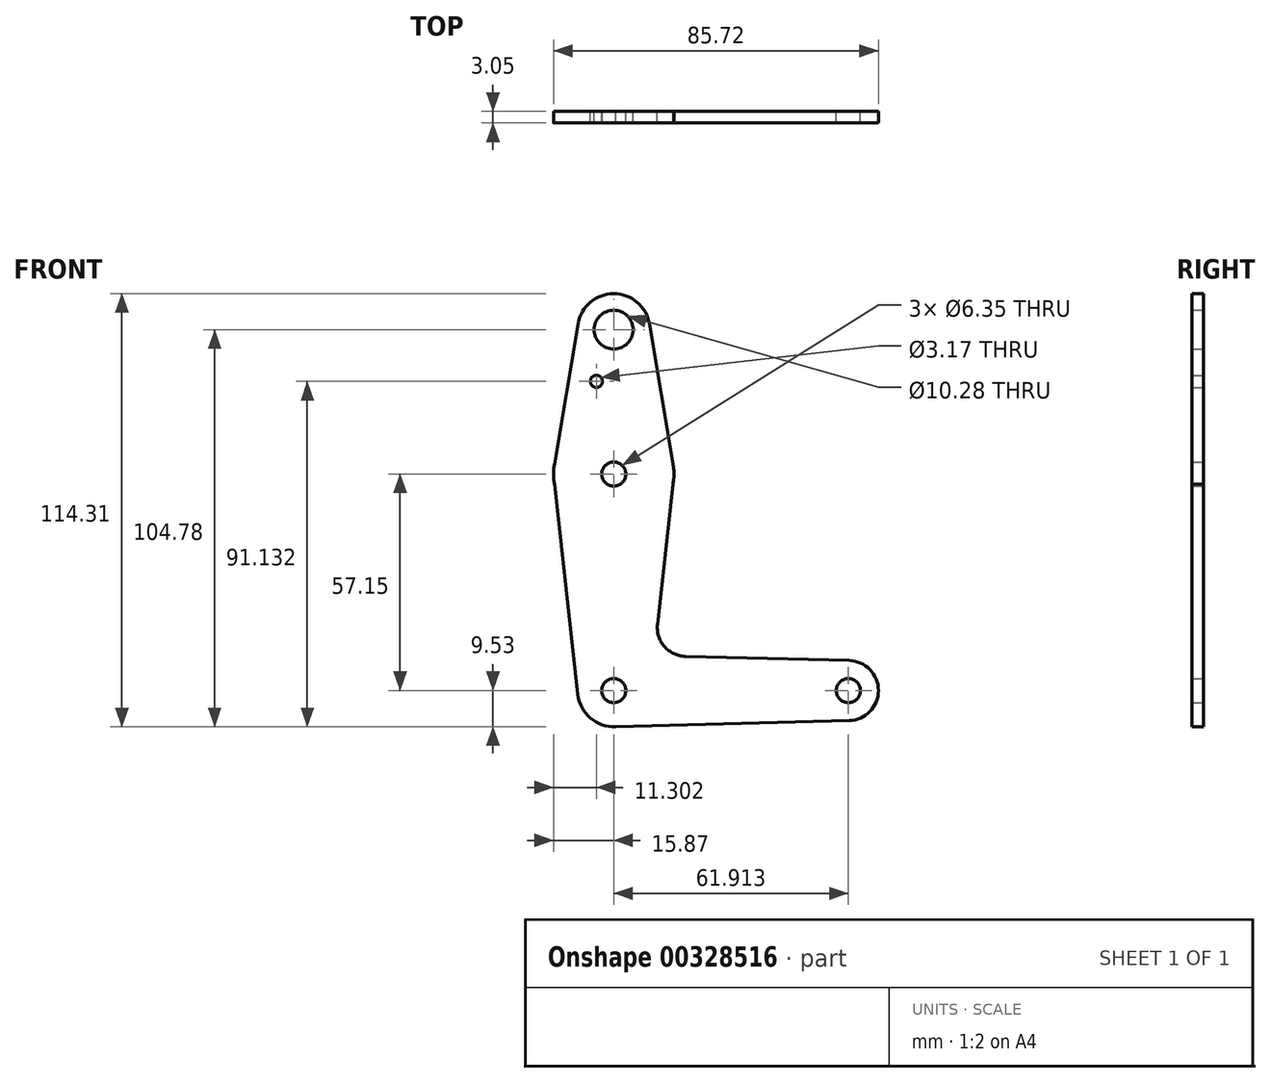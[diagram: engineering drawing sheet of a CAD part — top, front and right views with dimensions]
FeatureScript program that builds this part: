
annotation { "Feature Type Name" : "Feature", "Feature Type Description" : "" }
export const myFeature = defineFeature(function(context is Context, id is Id, definition is map)
    precondition{}
    {
        {
            var Q0;
            Q0=qCreatedBy(makeId("Front.planeOp"),FACE);
            var sketch = newSketch(context, id + "F0", { "sketchPlane" : qUnion([Q0])});
            skLineSegment(sketch, "E0", {"start": v(0, 0) * mm, "end": v(0, 95.25) * mm, "construction": true});
            skLineSegment(sketch, "E1", {"start": v(0, 0) * mm, "end": v(61.91, 0) * mm, "construction": true});
            skCircle(sketch, "E2", {"center": v(0, 95.25) * mm, "radius": 9.53 * mm});
            skCircle(sketch, "E3", {"center": v(0, 57.15) * mm, "radius": 15.88 * mm});
            skCircle(sketch, "E4", {"center": v(0, 0) * mm, "radius": 9.53 * mm});
            skCircle(sketch, "E5", {"center": v(61.91, 0) * mm, "radius": 7.94 * mm});
            skLineSegment(sketch, "E6", {"start": v(9.4, 96.84) * mm, "end": v(15.65, 59.8) * mm});
            skLineSegment(sketch, "E7", {"start": v(-15.65, 59.8) * mm, "end": v(-9.4, 96.84) * mm});
            skLineSegment(sketch, "E8", {"start": v(-15.65, 54.5) * mm, "end": v(-9.47, -1.05) * mm});
            skLineSegment(sketch, "E9", {"start": v(15.65, 54.5) * mm, "end": v(11.53, 17.5) * mm});
            skLineSegment(sketch, "E10", {"start": v(18.91, 9.04) * mm, "end": v(62.12, 7.93) * mm});
            skLineSegment(sketch, "E11", {"start": v(0, -9.52) * mm, "end": v(62.12, -7.93) * mm});
            skPoint(sketch, "E12.newPointA", {"position": v(9.47, -1.05) * mm});
            skArc(sketch, "E12.filletArc", {"start": v(11.53, 17.5) * mm, "mid": v(13.36, 11.65) * mm, "end": v(18.91, 9.04) * mm});
            skCircle(sketch, "E13", {"center": v(0, 95.25) * mm, "radius": 5.14 * mm});
            skCircle(sketch, "E14", {"center": v(-4.57, 81.6) * mm, "radius": 1.59 * mm});
            skCircle(sketch, "E15", {"center": v(0, 57.15) * mm, "radius": 3.18 * mm});
            skCircle(sketch, "E16", {"center": v(0, 0) * mm, "radius": 3.17 * mm});
            skCircle(sketch, "E17", {"center": v(61.91, 0) * mm, "radius": 3.18 * mm});
            skSolve(sketch);
        }
        {
            var Q0;
            Q0 = qSketchRegion(id + "F0", true);
            extrude(context, id + "F1", {"entities" : qUnion([Q0]), "depth" : 3.05 * mm});
        }
    });
